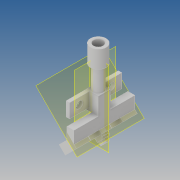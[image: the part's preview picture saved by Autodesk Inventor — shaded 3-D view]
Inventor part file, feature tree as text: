
AUTODESK INVENTOR PART (.ipt)
format: ipt  version: 2020 (Build 240168000, 168)  size: 536,064 bytes
history: native  units: mm
features: sketch x16, extrude x15, other x6, projected_geometry x4, revolve x1, chamfer x1
ambient origin geometry x8: Origin, YZ Plane, XZ Plane, XY Plane, X Axis, Y Axis, Z Axis, Center Point
bodies: Body1 (feature_tree)
feature tree (43):
  other  "솔리드1"
  extrude  "돌출1"  Depth=7.0mm
  extrude  "돌출2"  Depth=7.0mm
  extrude  "돌출3"  Depth=10.0mm TaperAngle=0.0deg
  other  "작업 평면1"
  revolve  "회전2"
  extrude  "돌출4"  Depth=6.0mm
  extrude  "돌출5"  Depth=13.0mm TaperAngle=0.0deg
  other  "작업 평면2"
  extrude  "돌출6"  Depth=9.0mm
  extrude  "돌출7"  Depth=10.0mm TaperAngle=0.0deg
  extrude  "돌출8"  Depth=2.75mm
  extrude  "돌출9"  Depth=5.0mm
  extrude  "돌출10"  Depth=2.5mm
  other  "작업 평면3"
  chamfer  "모따기1"  Distance=0.5mm
  extrude  "돌출12"  Depth=35.0mm
  extrude  "돌출13"  Depth=7.0mm
  extrude  "돌출14"  Depth=4.0mm TaperAngle=0.0deg
  extrude  "돌출15"  Depth=5.0mm
  extrude  "돌출16"  Depth=11.0mm TaperAngle=0.0deg
  sketch  "스케치1"
  sketch  "스케치2"
  sketch  "스케치3"
  sketch  "스케치4"
  projected_geometry  "투영된 루프1"
  sketch  "스케치5"
  sketch  "스케치6"
  sketch  "스케치7"
  projected_geometry  "투영된 루프2"
  sketch  "스케치8"
  sketch  "스케치9"
  sketch  "스케치10"
  sketch  "스케치11"
  sketch  "스케치13"
  sketch  "스케치14"
  sketch  "스케치15"
  sketch  "스케치16"
  sketch  "스케치17"
  projected_geometry  "투영된 루프3"
  projected_geometry  "투영된 루프4"
  other  "절단 모서리 투영1"
  other  "절단 모서리 투영2"
